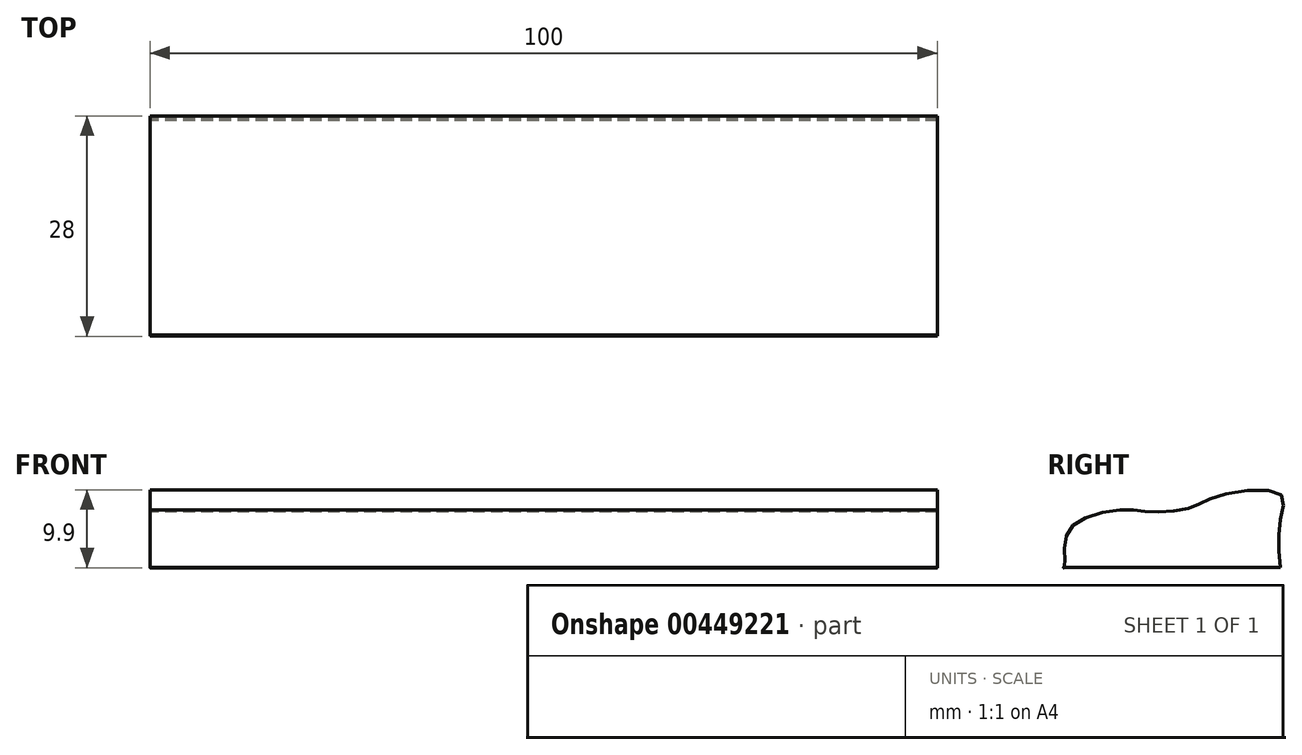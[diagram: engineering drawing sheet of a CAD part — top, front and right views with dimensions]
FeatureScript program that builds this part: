
annotation { "Feature Type Name" : "Feature", "Feature Type Description" : "" }
export const myFeature = defineFeature(function(context is Context, id is Id, definition is map)
    precondition{}
    {
        {
            var Q0;
            Q0=qCreatedBy(makeId("Right.planeOp"),FACE);
            var sketch = newSketch(context, id + "F0", { "sketchPlane" : qUnion([Q0])});
            skFitSpline(sketch, "E0", {"points": [v(0, 0) * mm, v(0, 5.9) * mm, v(0, 9.3) * mm, v(-8.15, 9.02) * mm, v(-11.27, 7.6) * mm, v(-16.37, 7.04) * mm, v(-19.76, 7.32) * mm, v(-26, 5.62) * mm, v(-27.41, 2.5) * mm, v(-27.41, 0) * mm, v(-27.7, 0) * mm], "startDerivative": vector(-4.17, 48.88) * mm, "endDerivative": vector(-12.1, 4.12) * mm});
            skLineSegment(sketch, "E1", {"start": v(0, 0) * mm, "end": v(-27.59, -0.04) * mm});
            skLineSegment(sketch, "E2", {"start": v(0, -11.9) * mm, "end": v(-26.34, -11.93) * mm});
            skSolve(sketch);
        }
        {
            var Q0;
            {var subQ0=sQuery(id+"F0.wireOp",EDGE,"E1");var subQ1=sQuery(id+"F0.wireOp",EDGE,"E0");var subQ2=makeQuery(id+"F0.imprint","INTERSECT",VERTEX,{"disambiguationData":[OD(1.0)],"derivedFrom":[subQ1,subQ0]});Q0=makeQuery(id+"F0.imprint","IMPRINT",FACE,{"disambiguationData":[TD([[makeQuery(id+"F0.imprint","IMPRINT",EDGE,{"disambiguationData":[TD([[subQ2,1.0]])],"derivedFrom":subQ1}),-1.0]])]});}
            var Q1;
            {var subQ0=sQuery(id+"F0.wireOp",EDGE,"E1");var subQ1=sQuery(id+"F0.wireOp",EDGE,"E0");var subQ2=makeQuery(id+"F0.imprint","INTERSECT",VERTEX,{"disambiguationData":[OD(0.0)],"derivedFrom":[subQ1,subQ0]});Q1=makeQuery(id+"F0.imprint","IMPRINT",FACE,{"disambiguationData":[TD([[makeQuery(id+"F0.imprint","IMPRINT",EDGE,{"disambiguationData":[TD([[subQ2,-1.0]])],"derivedFrom":subQ1}),1.0]])]});}
            extrude(context, id + "F1", {"entities" : qUnion([Q0, Q1]), "depth" : 100 * mm});
        }
    });
